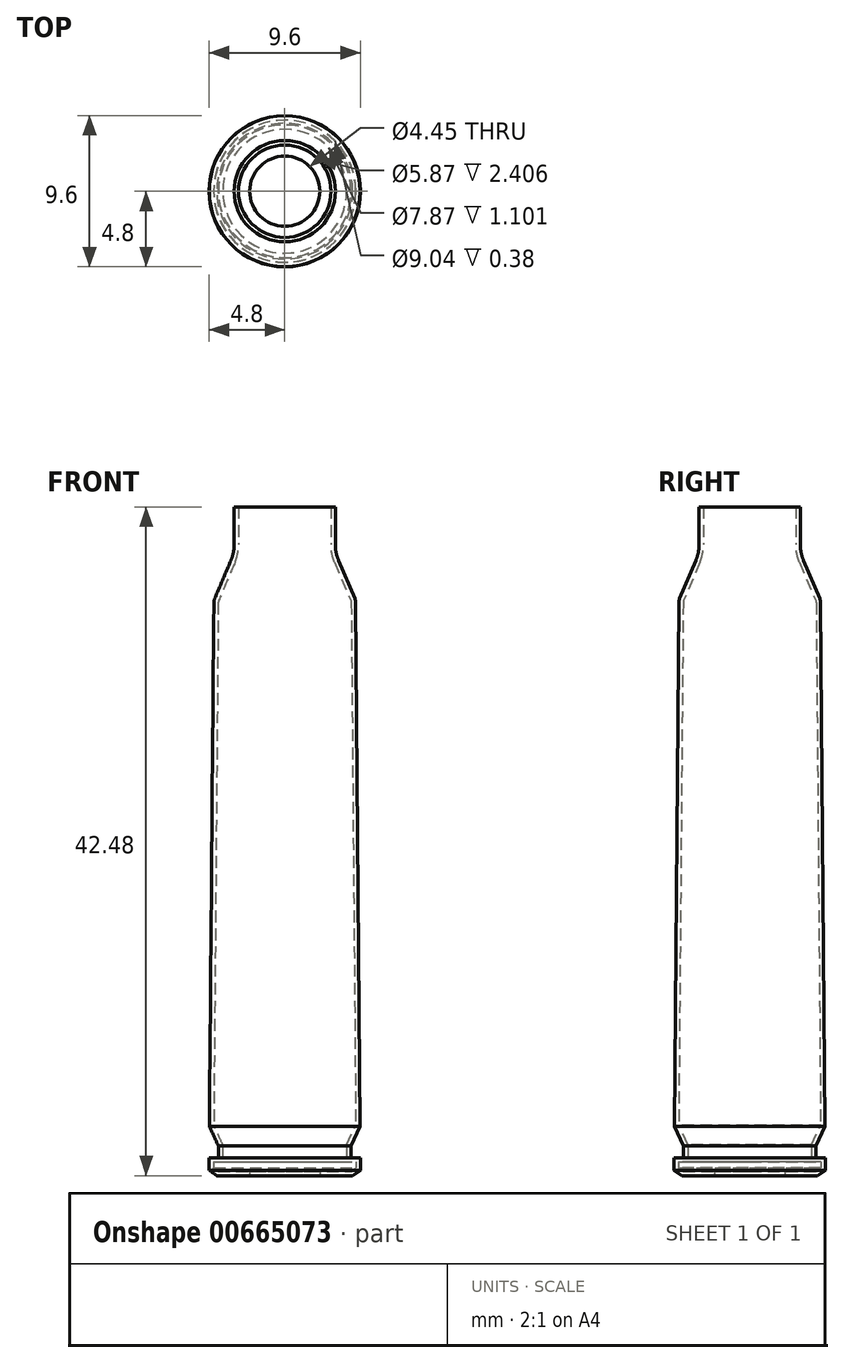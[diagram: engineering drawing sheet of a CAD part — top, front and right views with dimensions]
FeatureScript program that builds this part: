
annotation { "Feature Type Name" : "Feature", "Feature Type Description" : "" }
export const myFeature = defineFeature(function(context is Context, id is Id, definition is map)
    precondition{}
    {
        {
            var Q0;
            Q0=qCreatedBy(makeId("Front.planeOp"),FACE);
            var sketch = newSketch(context, id + "F0", { "sketchPlane" : qUnion([Q0])});
            skLineSegment(sketch, "E0", {"start": v(4.31, -41.16) * mm, "end": v(4.8, -40.82) * mm});
            skLineSegment(sketch, "E1", {"start": v(4.8, -40.82) * mm, "end": v(4.8, -40.01) * mm});
            skLineSegment(sketch, "E2", {"start": v(4.8, -40.01) * mm, "end": v(4.22, -40.01) * mm});
            skLineSegment(sketch, "E3", {"start": v(4.22, -40.01) * mm, "end": v(4.22, -39.25) * mm});
            skLineSegment(sketch, "E4", {"start": v(4.22, -39.25) * mm, "end": v(4.79, -38.02) * mm});
            skLineSegment(sketch, "E5", {"start": v(4.79, -38.02) * mm, "end": v(4.5, -4.76) * mm});
            skPoint(sketch, "E6", {"position": v(0, 5.97) * mm});
            skLineSegment(sketch, "E7", {"start": v(4.45, -4.52) * mm, "end": v(3.42, -2.08) * mm});
            skLineSegment(sketch, "E8", {"start": v(3.22, 1.32) * mm, "end": v(3.22, -1.09) * mm});
            skPoint(sketch, "E9.visualSharp", {"position": v(4.5, -4.63) * mm});
            skArc(sketch, "E9.filletArc", {"start": v(4.5, -4.76) * mm, "mid": v(4.49, -4.64) * mm, "end": v(4.45, -4.52) * mm});
            skPoint(sketch, "E10.visualSharp", {"position": v(3.22, -1.6) * mm});
            skArc(sketch, "E10.filletArc", {"start": v(3.22, -1.09) * mm, "mid": v(3.27, -1.6) * mm, "end": v(3.42, -2.08) * mm});
            skLineSegment(sketch, "E11", {"start": v(0, -41.15) * mm, "end": v(0, 1.32) * mm});
            skLineSegment(sketch, "E12", {"start": v(4.31, -41.16) * mm, "end": v(2.23, -41.16) * mm});
            skLineSegment(sketch, "E13.2", {"start": v(4.52, -40.3) * mm, "end": v(3.94, -40.3) * mm});
            skLineSegment(sketch, "E13.3", {"start": v(4.52, -40.67) * mm, "end": v(4.52, -40.3) * mm});
            skLineSegment(sketch, "E13.4", {"start": v(4.23, -40.88) * mm, "end": v(4.52, -40.67) * mm});
            skLineSegment(sketch, "E13.5", {"start": v(4.23, -40.88) * mm, "end": v(2.23, -40.88) * mm});
            skLineSegment(sketch, "E13.6", {"start": v(3.94, -40.3) * mm, "end": v(3.94, -39.2) * mm});
            skLineSegment(sketch, "E13.7", {"start": v(3.94, -39.2) * mm, "end": v(4.5, -37.96) * mm});
            skLineSegment(sketch, "E13.8", {"start": v(4.5, -37.96) * mm, "end": v(4.22, -4.76) * mm});
            skArc(sketch, "E13.9", {"start": v(4.22, -4.76) * mm, "mid": v(4.22, -4.7) * mm, "end": v(4.2, -4.63) * mm});
            skLineSegment(sketch, "E13.10", {"start": v(4.2, -4.63) * mm, "end": v(3.16, -2.19) * mm});
            skArc(sketch, "E13.11", {"start": v(2.94, -1.09) * mm, "mid": v(3, -1.65) * mm, "end": v(3.16, -2.19) * mm});
            skLineSegment(sketch, "E14", {"start": v(2.23, -41.16) * mm, "end": v(2.23, -40.88) * mm});
            skLineSegment(sketch, "E15", {"start": v(2.94, -1.09) * mm, "end": v(2.94, 1.32) * mm});
            skLineSegment(sketch, "E16", {"start": v(2.94, 1.32) * mm, "end": v(3.22, 1.32) * mm});
            skSolve(sketch);
        }
        {
            var Q0;
            Q0 = qSketchRegion(id + "F0", true);
            var Q1;
            Q1=sQuery(id+"F0.wireOp",EDGE,"E11");
            revolve(context, id + "F1", {"entities" : qUnion([Q0]), "axis" : qUnion([Q1]), "revolveType" : RevolveType.FULL});
        }
    });
